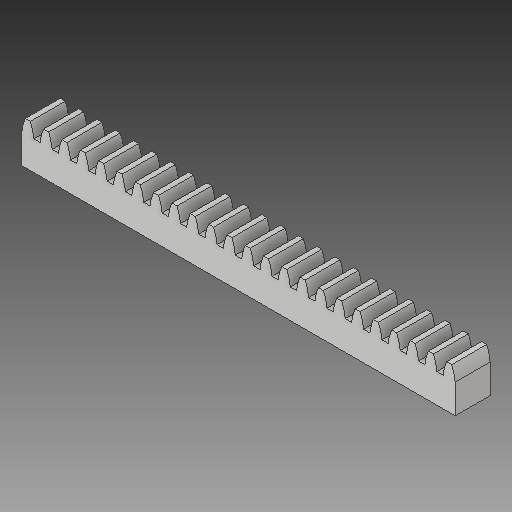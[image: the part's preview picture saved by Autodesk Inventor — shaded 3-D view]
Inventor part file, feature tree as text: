
AUTODESK INVENTOR PART (.ipt)
format: ipt  version: 2019 (Build 230136000, 136)  size: 202,240 bytes
history: native  units: mm
features: extrude x2, sketch x2, pattern_linear x1, projected_geometry x1
ambient origin geometry x8: Origin, YZ Plane, XZ Plane, XY Plane, X Axis, Y Axis, Z Axis, Center Point
bodies: Solid1 (feature_tree)
feature tree (6):
  extrude  "Extrusion1"  Depth=10.0mm
  extrude  "Extrusion2"  Depth=16.578504mm
  pattern_linear  "Rectangular Pattern1"  Spacing1=16.578504mm  [1 undecoded]
  sketch  "Sketch1"  dims[d0=148.627mm d1=10.0mm]
  sketch  "Sketch2"  dims[d2=12.0mm d3=0.0mm d4=16.578504mm d5=16.578504mm d6=22.0mm d7=28.84419mm d8=1.193189mm d9=6.418005mm d10=4.604341mm d11=1.193189mm d12=12.0mm d13=0.0mm d14=240.0mm d16=6.28318mm]
  projected_geometry  "Projected Loop1"
note: 1 required parameter value undecoded (feature->parameter linkage not recoverable at this tier; creation-order binding heuristic only, values carry confidence <= 0.55)
